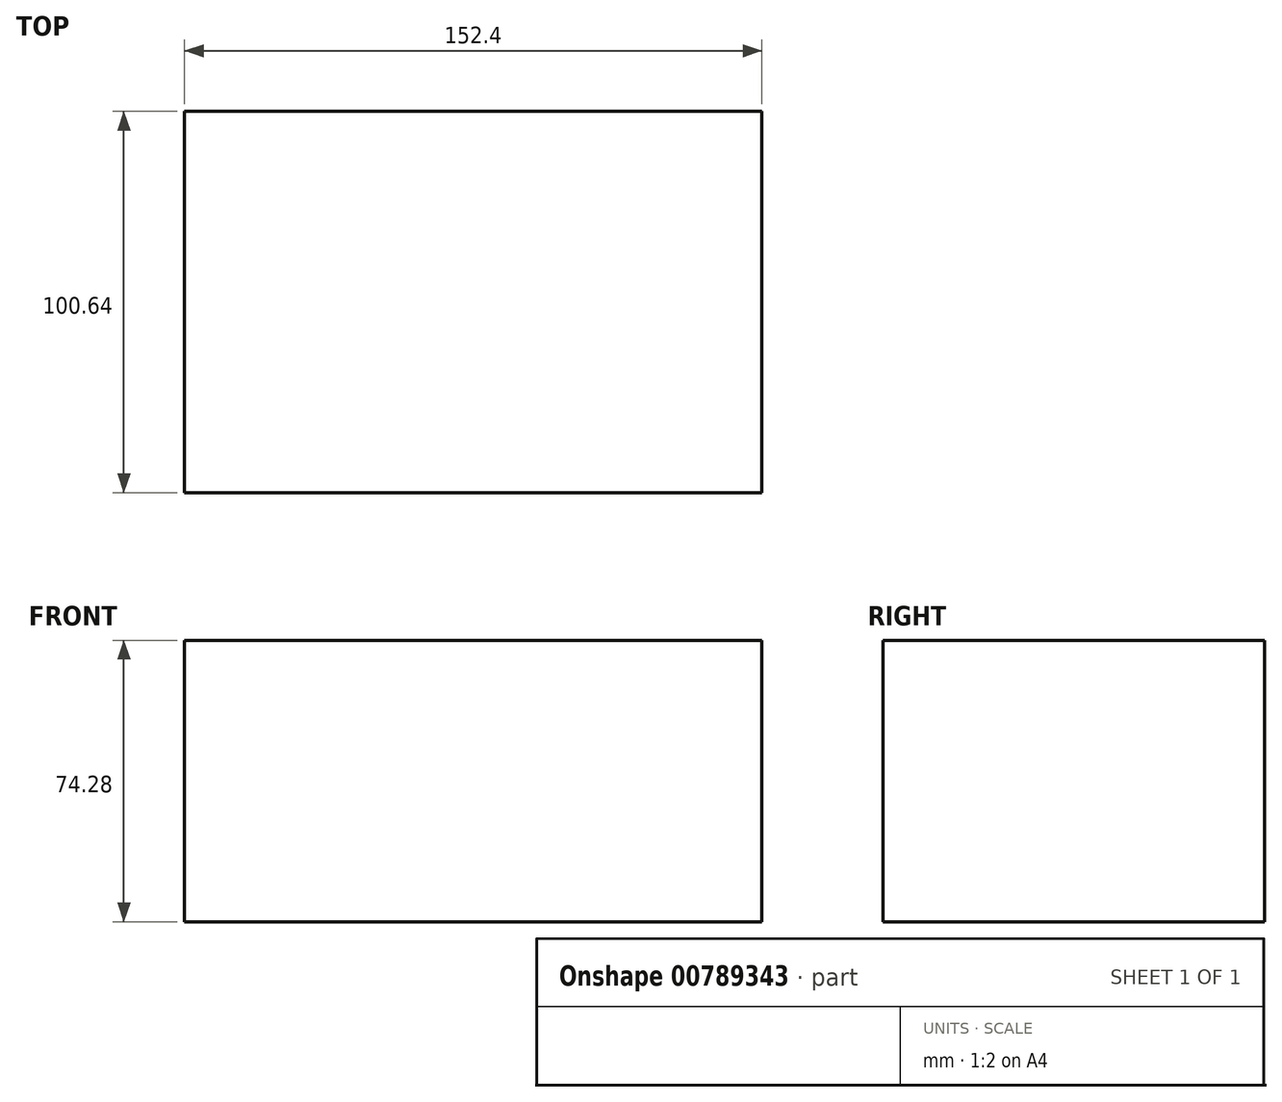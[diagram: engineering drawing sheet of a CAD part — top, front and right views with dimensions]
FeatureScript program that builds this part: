
annotation { "Feature Type Name" : "Feature", "Feature Type Description" : "" }
export const myFeature = defineFeature(function(context is Context, id is Id, definition is map)
    precondition{}
    {
        {
            var Q0;
            Q0=qCreatedBy(makeId("Right.planeOp"),FACE);
            var sketch = newSketch(context, id + "F0", { "sketchPlane" : qUnion([Q0])});
            skLineSegment(sketch, "E0.bottom", {"start": v(50.32, 37.14) * mm, "end": v(-50.32, 37.14) * mm});
            skLineSegment(sketch, "E0.top", {"start": v(50.32, -37.14) * mm, "end": v(-50.32, -37.14) * mm});
            skLineSegment(sketch, "E0.left", {"start": v(50.32, 37.14) * mm, "end": v(50.32, -37.14) * mm});
            skLineSegment(sketch, "E0.right", {"start": v(-50.32, 37.14) * mm, "end": v(-50.32, -37.14) * mm});
            skPoint(sketch, "E0.middle", {"position": v(0, 0) * mm});
            skSolve(sketch);
        }
        {
            var Q0;
            Q0 = qSketchRegion(id + "F0", true);
            extrude(context, id + "F1", {"entities" : qUnion([Q0]), "depth" : 152.4 * mm, "offsetDistance" : 25.4 * mm});
        }
    });
